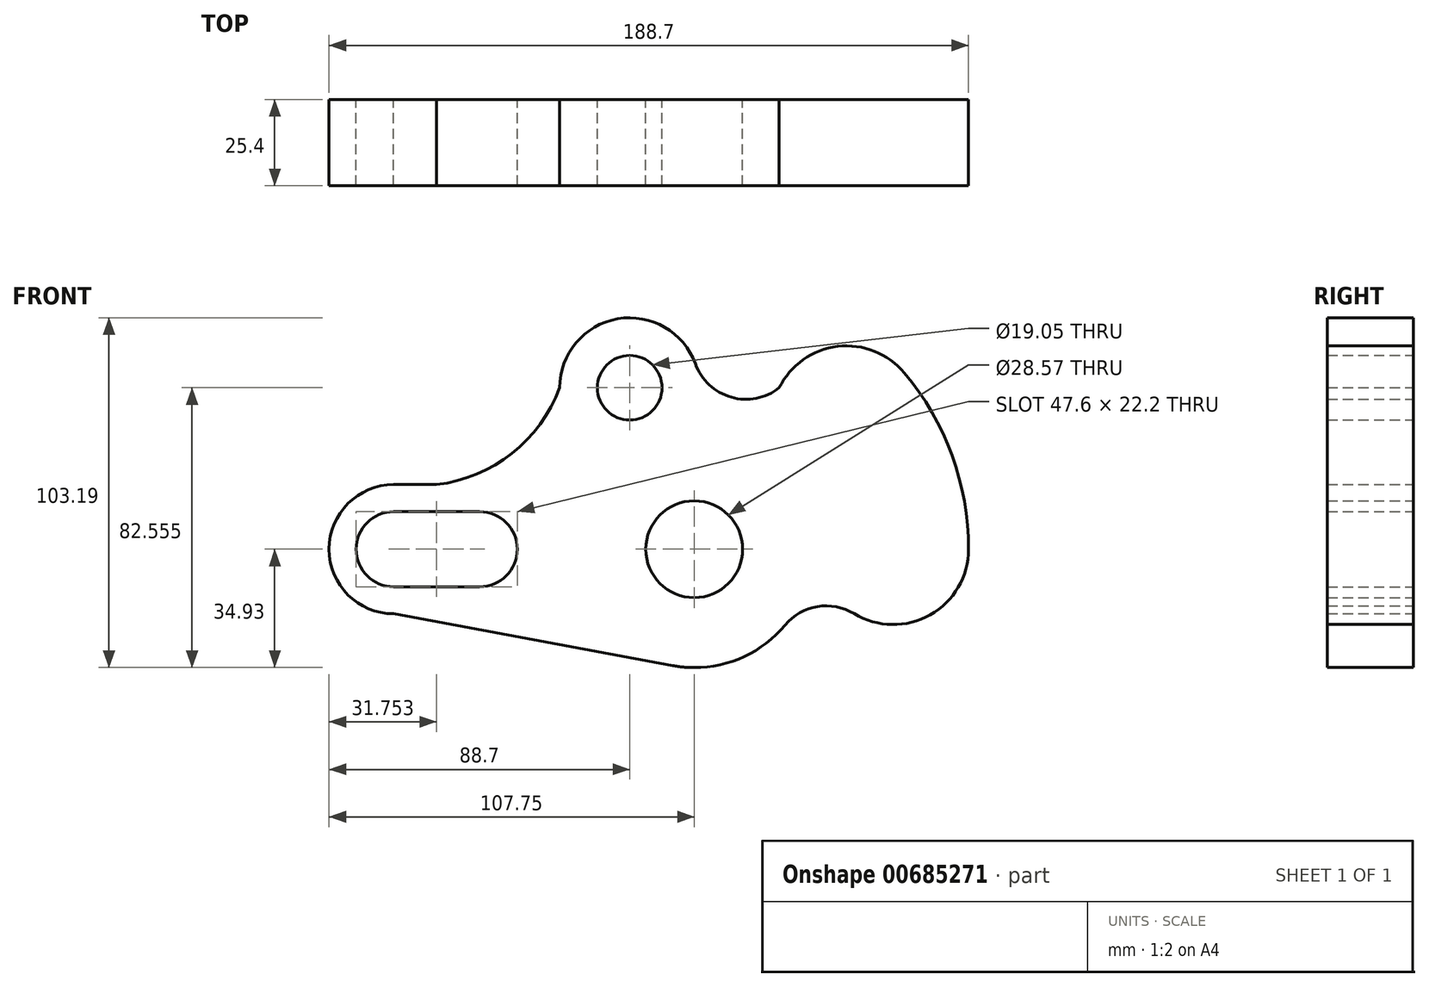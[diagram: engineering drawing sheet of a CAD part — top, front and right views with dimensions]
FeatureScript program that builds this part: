
annotation { "Feature Type Name" : "Feature", "Feature Type Description" : "" }
export const myFeature = defineFeature(function(context is Context, id is Id, definition is map)
    precondition{}
    {
        {
            var Q0;
            Q0=qCreatedBy(makeId("Front.planeOp"),FACE);
            var sketch = newSketch(context, id + "F0", { "sketchPlane" : qUnion([Q0])});
            skCircle(sketch, "E0", {"center": v(0, 0) * mm, "radius": 14.29 * mm});
            skCircle(sketch, "E1", {"center": v(0, 0) * mm, "radius": 22.23 * mm});
            skCircle(sketch, "E2", {"center": v(-19.05, 47.62) * mm, "radius": 9.53 * mm});
            skCircle(sketch, "E3", {"center": v(-19.05, 47.62) * mm, "radius": 20.64 * mm});
            skArc(sketch, "E4", {"start": v(-88.7, 11.1) * mm, "mid": v(-99.8, 0) * mm, "end": v(-88.7, -11.1) * mm});
            skArc(sketch, "E5", {"start": v(-63.3, -11.1) * mm, "mid": v(-52.2, 0) * mm, "end": v(-63.3, 11.1) * mm});
            skLineSegment(sketch, "E6", {"start": v(-88.7, 11.1) * mm, "end": v(-63.3, 11.1) * mm});
            skLineSegment(sketch, "E7", {"start": v(-88.7, -11.1) * mm, "end": v(-63.3, -11.1) * mm});
            skArc(sketch, "E8", {"start": v(47.2, -19) * mm, "mid": v(69.63, -19.36) * mm, "end": v(80.95, 0) * mm});
            skLineSegment(sketch, "E9", {"start": v(0, 0) * mm, "end": v(89.97, 75.5) * mm, "construction": true});
            skLineSegment(sketch, "E10", {"start": v(0, 0) * mm, "end": v(110.19, 0) * mm, "construction": true});
            skArc(sketch, "E11", {"start": v(0, -34.93) * mm, "mid": v(14.79, -31.64) * mm, "end": v(26.8, -22.4) * mm});
            skArc(sketch, "E12.filletArc", {"start": v(47.2, -19) * mm, "mid": v(36.37, -16.92) * mm, "end": v(26.8, -22.4) * mm});
            skArc(sketch, "E13", {"start": v(47.6, 0) * mm, "mid": v(58.72, -11.13) * mm, "end": v(69.85, 0) * mm});
            skArc(sketch, "E14", {"start": v(53.5, 44.9) * mm, "mid": v(37.83, 46.27) * mm, "end": v(36.46, 30.6) * mm});
            skArc(sketch, "E15", {"start": v(62.01, 52.03) * mm, "mid": v(42.35, 59.82) * mm, "end": v(25.08, 47.62) * mm});
            skLineSegment(sketch, "E16", {"start": v(0, 0) * mm, "end": v(-125.57, 0) * mm, "construction": true});
            skLineSegment(sketch, "E17", {"start": v(0, 0) * mm, "end": v(0, 0) * mm, "construction": true});
            skArc(sketch, "E18.trimOffspring", {"start": v(0, 58.72) * mm, "mid": v(-0.82, 58.72) * mm, "end": v(-1.64, 58.7) * mm, "construction": true});
            skArc(sketch, "E19", {"start": v(36.46, 30.6) * mm, "mid": v(44.73, 16.28) * mm, "end": v(47.6, 0) * mm});
            skArc(sketch, "E20", {"start": v(53.5, 44.9) * mm, "mid": v(65.64, 23.9) * mm, "end": v(69.85, 0) * mm});
            skArc(sketch, "E21", {"start": v(62.01, 52.03) * mm, "mid": v(76.07, 27.69) * mm, "end": v(80.95, 0) * mm});
            skLineSegment(sketch, "E22.trimOffspring", {"start": v(0, 14.29) * mm, "end": v(0, 22.23) * mm, "construction": true});
            skLineSegment(sketch, "E23.trimOffspring", {"start": v(0, -14.29) * mm, "end": v(0, -22.23) * mm, "construction": true});
            skArc(sketch, "E24", {"start": v(-63.3, -19.05) * mm, "mid": v(-44.25, 0) * mm, "end": v(-63.3, 19.05) * mm});
            skLineSegment(sketch, "E25", {"start": v(-88.7, 19.05) * mm, "end": v(-63.3, 19.05) * mm});
            skLineSegment(sketch, "E26", {"start": v(-88.7, -19.05) * mm, "end": v(-63.3, -19.05) * mm});
            skLineSegment(sketch, "E27", {"start": v(-76, 0) * mm, "end": v(-76, 37.27) * mm, "construction": true});
            skPoint(sketch, "E27.startSnap0", {"position": v(-76, 11.1) * mm});
            skPoint(sketch, "E27.endSnap0", {"position": v(-76, 19.05) * mm});
            skArc(sketch, "E28.MirrorCS", {"start": v(-88.7, -19.05) * mm, "mid": v(-107.75, 0) * mm, "end": v(-88.7, 19.05) * mm});
            skArc(sketch, "E29", {"start": v(-76, 19.05) * mm, "mid": v(-53.84, 28.25) * mm, "end": v(-39.69, 47.62) * mm});
            skArc(sketch, "E30", {"start": v(-6.38, -34.34) * mm, "mid": v(11.88, -32.84) * mm, "end": v(26.86, -22.32) * mm});
            skLineSegment(sketch, "E31", {"start": v(-88.7, -19.05) * mm, "end": v(-6.38, -34.34) * mm});
            skArc(sketch, "E32", {"start": v(0.34, 54.68) * mm, "mid": v(10.91, 44.84) * mm, "end": v(25.08, 47.62) * mm});
            skSolve(sketch);
        }
        {
            var Q0;
            Q0=makeQuery(id+"F0.imprint","IMPRINT",FACE,{"disambiguationData":[TD([[makeQuery(id+"F0.imprint","IMPRINT",EDGE,{"derivedFrom":sQuery(id+"F0.wireOp",EDGE,"E2")}),-1.0]])]});
            var Q1;
            Q1=makeQuery(id+"F0.imprint","IMPRINT",FACE,{"disambiguationData":[TD([[makeQuery(id+"F0.imprint","IMPRINT",EDGE,{"derivedFrom":sQuery(id+"F0.wireOp",EDGE,"E4")}),-1.0]])]});
            var Q2;
            Q2=makeQuery(id+"F0.imprint","IMPRINT",FACE,{"disambiguationData":[TD([[makeQuery(id+"F0.imprint","IMPRINT",EDGE,{"derivedFrom":sQuery(id+"F0.wireOp",EDGE,"E0")}),-1.0]])]});
            var Q3;
            Q3=makeQuery(id+"F0.imprint","IMPRINT",FACE,{"disambiguationData":[TD([[makeQuery(id+"F0.imprint","IMPRINT",EDGE,{"derivedFrom":sQuery(id+"F0.wireOp",EDGE,"E1")}),-1.0]])]});
            extrude(context, id + "F1", {"entities" : qUnion([Q0, Q1, Q2, Q3]), "endBound" : BoundingType.SYMMETRIC, "depth" : 25.4 * mm, "offsetDistance" : 25.4 * mm});
        }
        {
            var Q0;
            Q0=sQuery(id+"F0.wireOp",EDGE,"E24");
            var Q1;
            Q1=sQuery(id+"F0.wireOp",EDGE,"E25");
            var Q2;
            Q2=sQuery(id+"F0.wireOp",EDGE,"E26");
            var Q3;
            Q3=sQuery(id+"F0.wireOp",EDGE,"E28.MirrorCS");
            var Q4;
            Q4=sQuery(id+"F0.wireOp",EDGE,"E4");
            var Q5;
            Q5=sQuery(id+"F0.wireOp",EDGE,"E7");
            var Q6;
            Q6=sQuery(id+"F0.wireOp",EDGE,"E5");
            var Q7;
            Q7=sQuery(id+"F0.wireOp",EDGE,"E6");
            var Q8;
            Q8=sQuery(id+"F0.wireOp",EDGE,"E1");
            var Q9;
            Q9=sQuery(id+"F0.wireOp",EDGE,"E0");
            var Q10;
            Q10=sQuery(id+"F0.wireOp",EDGE,"E2");
            var Q11;
            Q11=sQuery(id+"F0.wireOp",EDGE,"E3");
            extrude(context, id + "F2", {"bodyType" : ToolBodyType.SURFACE, "operationType" : NewBodyOperationType.ADD, "surfaceEntities" : qUnion([Q0, Q1, Q2, Q3, Q4, Q5, Q6, Q7, Q8, Q9, Q10, Q11]), "endBound" : BoundingType.SYMMETRIC, "depth" : 44.45 * mm, "offsetDistance" : 25.4 * mm});
        }
    });
